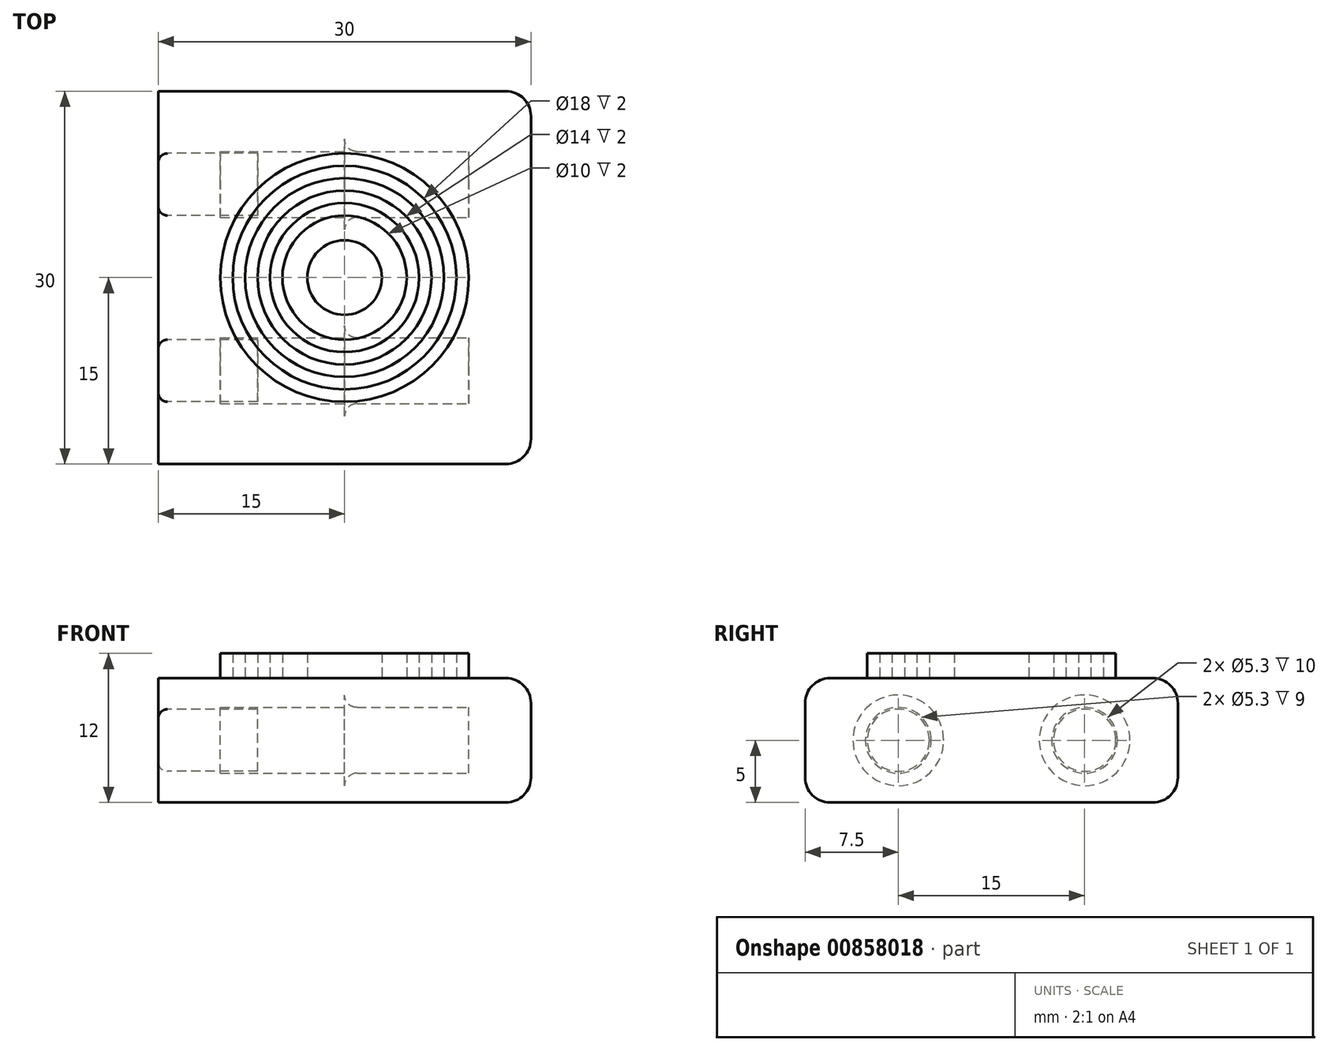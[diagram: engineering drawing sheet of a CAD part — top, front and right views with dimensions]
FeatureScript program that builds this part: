
annotation { "Feature Type Name" : "Feature", "Feature Type Description" : "" }
export const myFeature = defineFeature(function(context is Context, id is Id, definition is map)
    precondition{}
    {
        {
            var Q0;
            Q0=qCreatedBy(makeId("Right.planeOp"),FACE);
            var sketch = newSketch(context, id + "F0", { "sketchPlane" : qUnion([Q0])});
            skLineSegment(sketch, "E0.bottom", {"start": v(-15, 5) * mm, "end": v(15, 5) * mm});
            skLineSegment(sketch, "E0.top", {"start": v(-15, -5) * mm, "end": v(15, -5) * mm});
            skLineSegment(sketch, "E0.left", {"start": v(-15, 5) * mm, "end": v(-15, -5) * mm});
            skLineSegment(sketch, "E0.right", {"start": v(15, 5) * mm, "end": v(15, -5) * mm});
            skPoint(sketch, "E0.middle", {"position": v(0, 0) * mm});
            skLineSegment(sketch, "E1", {"start": v(-15, 0) * mm, "end": v(0, 0) * mm, "construction": true});
            skLineSegment(sketch, "E2", {"start": v(0, 0) * mm, "end": v(15, 0) * mm, "construction": true});
            skCircle(sketch, "E3", {"center": v(-7.5, 0) * mm, "radius": 2.65 * mm});
            skCircle(sketch, "E4", {"center": v(7.5, 0) * mm, "radius": 2.65 * mm});
            skSolve(sketch);
        }
        {
            var Q0;
            Q0=makeQuery(id+"F0.imprint","IMPRINT",FACE,{"disambiguationData":[TD([[makeQuery(id+"F0.imprint","IMPRINT",EDGE,{"derivedFrom":sQuery(id+"F0.wireOp",EDGE,"E0.bottom")}),-1.0]])]});
            var Q1;
            Q1=makeQuery(id+"F0.imprint","IMPRINT",FACE,{"disambiguationData":[TD([[makeQuery(id+"F0.imprint","IMPRINT",EDGE,{"derivedFrom":sQuery(id+"F0.wireOp",EDGE,"E4")}),1.0]])]});
            var Q2;
            Q2=makeQuery(id+"F0.imprint","IMPRINT",FACE,{"disambiguationData":[TD([[makeQuery(id+"F0.imprint","IMPRINT",EDGE,{"derivedFrom":sQuery(id+"F0.wireOp",EDGE,"E3")}),1.0]])]});
            extrude(context, id + "F1", {"entities" : qUnion([Q0, Q1, Q2]), "endBound" : BoundingType.SYMMETRIC, "depth" : 20 * mm, "offsetDistance" : 25 * mm});
        }
        {
            var Q0;
            Q0=makeQuery(id+"F1.opExtrude","SWEPT_BODY",BODY,{"disambiguationData":[OSD([sQuery(id+"F0.wireOp",EDGE,"E0.bottom"),sQuery(id+"F0.wireOp",EDGE,"E0.top"),sQuery(id+"F0.wireOp",EDGE,"E0.left"),sQuery(id+"F0.wireOp",EDGE,"E0.right")])]});
            transform(context, id + "F2", {"entities" : qUnion([Q0]), "transformType" : TransformType.TRANSLATION_3D, "dx" : -25 * mm, "dy" : 0 * mm, "dz" : 0 * mm, "makeCopy" : true});
        }
        {
            var Q0;
            Q0=makeQuery(id+"F2.opPattern","COPY",FACE,{"derivedFrom":makeQuery(id+"F1.opExtrude","CAP_FACE",FACE,{"disambiguationData":[OSD([sQuery(id+"F0.wireOp",EDGE,"E0.bottom"),sQuery(id+"F0.wireOp",EDGE,"E0.top"),sQuery(id+"F0.wireOp",EDGE,"E0.left"),sQuery(id+"F0.wireOp",EDGE,"E0.right")])],"isStart":true}),"instanceName":"1"});
            extrude(context, id + "F3", {"entities" : qUnion([Q0]), "operationType" : NewBodyOperationType.REMOVE, "oppositeDirection" : true, "depth" : 5 * mm, "offsetDistance" : 25 * mm});
        }
        {
            var Q0;
            Q0=makeQuery(id+"F1.opExtrude","CAP_FACE",FACE,{"disambiguationData":[OSD([sQuery(id+"F0.wireOp",EDGE,"E0.bottom"),sQuery(id+"F0.wireOp",EDGE,"E0.top"),sQuery(id+"F0.wireOp",EDGE,"E0.left"),sQuery(id+"F0.wireOp",EDGE,"E0.right")])],"isStart":false});
            extrude(context, id + "F4", {"entities" : qUnion([Q0]), "operationType" : NewBodyOperationType.REMOVE, "oppositeDirection" : true, "depth" : 5 * mm, "offsetDistance" : 25 * mm});
        }
        {
            var Q0;
            Q0=makeQuery(id+"F0.imprint","IMPRINT",FACE,{"disambiguationData":[TD([[makeQuery(id+"F0.imprint","IMPRINT",EDGE,{"derivedFrom":sQuery(id+"F0.wireOp",EDGE,"E4")}),1.0]])]});
            var Q1;
            Q1=makeQuery(id+"F0.imprint","IMPRINT",FACE,{"disambiguationData":[TD([[makeQuery(id+"F0.imprint","IMPRINT",EDGE,{"derivedFrom":sQuery(id+"F0.wireOp",EDGE,"E3")}),1.0]])]});
            extrude(context, id + "F5", {"entities" : qUnion([Q0, Q1]), "operationType" : NewBodyOperationType.REMOVE, "oppositeDirection" : true, "depth" : 25 * mm, "offsetDistance" : 25 * mm});
        }
        {
            var Q0;
            Q0=makeQuery(id+"F5.boolean.opBoolean","INTERSECT",EDGE,{"derivedFrom":[makeQuery(id+"F1.opExtrude","CAP_FACE",FACE,{"disambiguationData":[OSD([sQuery(id+"F0.wireOp",EDGE,"E0.bottom"),sQuery(id+"F0.wireOp",EDGE,"E0.top"),sQuery(id+"F0.wireOp",EDGE,"E0.left"),sQuery(id+"F0.wireOp",EDGE,"E0.right")])],"isStart":true}),makeQuery(id+"F5.opExtrude","SWEPT_FACE",FACE,{"disambiguationData":[OSD([sQuery(id+"F0.wireOp",EDGE,"E4")])]})]});
            var Q1;
            Q1=makeQuery(id+"F5.boolean.opBoolean","INTERSECT",EDGE,{"derivedFrom":[makeQuery(id+"F1.opExtrude","CAP_FACE",FACE,{"disambiguationData":[OSD([sQuery(id+"F0.wireOp",EDGE,"E0.bottom"),sQuery(id+"F0.wireOp",EDGE,"E0.top"),sQuery(id+"F0.wireOp",EDGE,"E0.left"),sQuery(id+"F0.wireOp",EDGE,"E0.right")])],"isStart":true}),makeQuery(id+"F5.opExtrude","SWEPT_FACE",FACE,{"disambiguationData":[OSD([sQuery(id+"F0.wireOp",EDGE,"E3")])]})]});
            fillet(context, id + "F6", {"entities" : qUnion([Q0, Q1]), "radius" : 1 * mm, "tangentPropagation" : true, "allowEdgeOverflow" : false});
        }
        {
            var Q0;
            Q0=makeQuery(id+"F2.opPattern","COPY",FACE,{"derivedFrom":makeQuery(id+"F1.opExtrude","CAP_FACE",FACE,{"disambiguationData":[OSD([sQuery(id+"F0.wireOp",EDGE,"E0.bottom"),sQuery(id+"F0.wireOp",EDGE,"E0.top"),sQuery(id+"F0.wireOp",EDGE,"E0.left"),sQuery(id+"F0.wireOp",EDGE,"E0.right")])],"isStart":false}),"instanceName":"1"});
            var sketch = newSketch(context, id + "F7", { "sketchPlane" : qUnion([Q0])});
            skLineSegment(sketch, "E5.bottom", {"start": v(-15, 5) * mm, "end": v(15, 5) * mm});
            skLineSegment(sketch, "E5.top", {"start": v(-15, -5) * mm, "end": v(15, -5) * mm});
            skLineSegment(sketch, "E5.left", {"start": v(-15, 5) * mm, "end": v(-15, -5) * mm});
            skLineSegment(sketch, "E5.right", {"start": v(15, 5) * mm, "end": v(15, -5) * mm});
            skPoint(sketch, "E5.middle", {"position": v(0, 0) * mm});
            skLineSegment(sketch, "E6", {"start": v(-15, 0) * mm, "end": v(0, 0) * mm, "construction": true});
            skLineSegment(sketch, "E7", {"start": v(0, 0) * mm, "end": v(15, 0) * mm, "construction": true});
            skCircle(sketch, "E8", {"center": v(-7.5, 0) * mm, "radius": 2.5 * mm});
            skCircle(sketch, "E9", {"center": v(7.5, 0) * mm, "radius": 2.5 * mm});
            skSolve(sketch);
        }
        {
            var Q0;
            Q0=makeQuery(id+"F7.imprint","IMPRINT",FACE,{"disambiguationData":[TD([[makeQuery(id+"F7.imprint","IMPRINT",EDGE,{"derivedFrom":sQuery(id+"F7.wireOp",EDGE,"E8")}),1.0]])]});
            var Q1;
            Q1=makeQuery(id+"F7.imprint","IMPRINT",FACE,{"disambiguationData":[TD([[makeQuery(id+"F7.imprint","IMPRINT",EDGE,{"derivedFrom":sQuery(id+"F7.wireOp",EDGE,"E9")}),1.0]])]});
            extrude(context, id + "F8", {"entities" : qUnion([Q0, Q1]), "operationType" : NewBodyOperationType.ADD, "depth" : 8 * mm, "offsetDistance" : 25 * mm});
        }
        {
            var Q0;
            Q0=makeQuery(id+"F8.opExtrude","CAP_EDGE",EDGE,{"disambiguationData":[OSD([sQuery(id+"F7.wireOp",EDGE,"E8")])],"isStart":true});
            var Q1;
            Q1=makeQuery(id+"F8.opExtrude","CAP_EDGE",EDGE,{"disambiguationData":[OSD([sQuery(id+"F7.wireOp",EDGE,"E9")])],"isStart":true});
            fillet(context, id + "F9", {"entities" : qUnion([Q0, Q1]), "radius" : 0.75 * mm, "tangentPropagation" : true, "allowEdgeOverflow" : false});
        }
        {
            var Q0;
            Q0=makeQuery(id+"F1.opExtrude","SWEPT_BODY",BODY,{"disambiguationData":[OSD([sQuery(id+"F0.wireOp",EDGE,"E0.bottom"),sQuery(id+"F0.wireOp",EDGE,"E0.top"),sQuery(id+"F0.wireOp",EDGE,"E0.left"),sQuery(id+"F0.wireOp",EDGE,"E0.right")])]});
            var Q1;
            Q1=qCreatedBy(makeId("Right.planeOp"),FACE);
            transform(context, id + "F10", {"entities" : qUnion([Q0]), "transformType" : TransformType.TRANSLATION_DISTANCE, "transformDirection" : qUnion([Q1]), "distance" : 10 * mm, "makeCopy" : false});
        }
        {
            var Q0;
            Q0=makeQuery(id+"F2.opPattern","COPY",BODY,{"derivedFrom":makeQuery(id+"F1.opExtrude","SWEPT_BODY",BODY,{"disambiguationData":[OSD([sQuery(id+"F0.wireOp",EDGE,"E0.bottom"),sQuery(id+"F0.wireOp",EDGE,"E0.top"),sQuery(id+"F0.wireOp",EDGE,"E0.left"),sQuery(id+"F0.wireOp",EDGE,"E0.right")])]}),"instanceName":"1"});
            var Q1;
            Q1=qCreatedBy(makeId("Right.planeOp"),FACE);
            transform(context, id + "F11", {"entities" : qUnion([Q0]), "transformType" : TransformType.TRANSLATION_DISTANCE, "transformDirection" : qUnion([Q1]), "distance" : 15 * mm, "makeCopy" : false});
        }
        {
            var Q0;
            Q0=makeQuery(id+"F1.opExtrude","SWEPT_FACE",FACE,{"disambiguationData":[OSD([sQuery(id+"F0.wireOp",EDGE,"E0.bottom")])]});
            var sketch = newSketch(context, id + "F12", { "sketchPlane" : qUnion([Q0])});
            skCircle(sketch, "E10", {"center": v(0, 0) * mm, "radius": 10 * mm});
            skCircle(sketch, "E11", {"center": v(0, 0) * mm, "radius": 9 * mm});
            skCircle(sketch, "E12", {"center": v(0, 0) * mm, "radius": 8 * mm});
            skCircle(sketch, "E13", {"center": v(0, 0) * mm, "radius": 7 * mm});
            skCircle(sketch, "E14", {"center": v(0, 0) * mm, "radius": 6 * mm});
            skCircle(sketch, "E15", {"center": v(0, 0) * mm, "radius": 5 * mm});
            skLineSegment(sketch, "E16", {"start": v(0, 10) * mm, "end": v(0, -10) * mm});
            skCircle(sketch, "E17", {"center": v(0, 0) * mm, "radius": 3 * mm});
            skSolve(sketch);
        }
        {
            var Q0;
            {var subQ0=sQuery(id+"F12.wireOp",EDGE,"E16");var subQ5=sQuery(id+"F12.wireOp",EDGE,"E11");var subQ6=makeQuery(id+"F12.imprint","INTERSECT",VERTEX,{"disambiguationData":[OD(0.0)],"derivedFrom":[subQ5,subQ0]});Q0=makeQuery(id+"F12.imprint","IMPRINT",FACE,{"disambiguationData":[TD([[makeQuery(id+"F12.imprint","IMPRINT",EDGE,{"disambiguationData":[TD([[subQ6,-1.0]])],"derivedFrom":subQ5}),-1.0]])]});}
            var Q1;
            {var subQ0=sQuery(id+"F12.wireOp",EDGE,"E16");var subQ1=sQuery(id+"F12.wireOp",EDGE,"E12");var subQ2=makeQuery(id+"F12.imprint","INTERSECT",VERTEX,{"disambiguationData":[OD(0.0)],"derivedFrom":[subQ1,subQ0]});Q1=makeQuery(id+"F12.imprint","IMPRINT",FACE,{"disambiguationData":[TD([[makeQuery(id+"F12.imprint","IMPRINT",EDGE,{"disambiguationData":[TD([[subQ2,-1.0]])],"derivedFrom":subQ1}),1.0]])]});}
            var Q2;
            {var subQ0=sQuery(id+"F12.wireOp",EDGE,"E16");var subQ1=sQuery(id+"F12.wireOp",EDGE,"E14");var subQ2=makeQuery(id+"F12.imprint","INTERSECT",VERTEX,{"disambiguationData":[OD(0.0)],"derivedFrom":[subQ1,subQ0]});Q2=makeQuery(id+"F12.imprint","IMPRINT",FACE,{"disambiguationData":[TD([[makeQuery(id+"F12.imprint","IMPRINT",EDGE,{"disambiguationData":[TD([[subQ2,-1.0]])],"derivedFrom":subQ1}),1.0]])]});}
            var Q3;
            {var subQ0=sQuery(id+"F12.wireOp",EDGE,"E17");var subQ1=sQuery(id+"F12.wireOp",EDGE,"E16");var subQ2=makeQuery(id+"F12.imprint","INTERSECT",VERTEX,{"disambiguationData":[OD(0.0)],"derivedFrom":[subQ1,subQ0]});Q3=makeQuery(id+"F12.imprint","IMPRINT",FACE,{"disambiguationData":[TD([[makeQuery(id+"F12.imprint","IMPRINT",EDGE,{"disambiguationData":[TD([[subQ2,-1.0]])],"derivedFrom":subQ1}),-1.0]])]});}
            extrude(context, id + "F13", {"entities" : qUnion([Q0, Q1, Q2, Q3]), "operationType" : NewBodyOperationType.ADD, "depth" : 2 * mm, "offsetDistance" : 25 * mm});
        }
        {
            var Q0;
            {var subQ0=sQuery(id+"F12.wireOp",EDGE,"E16");var subQ5=sQuery(id+"F12.wireOp",EDGE,"E11");var subQ6=makeQuery(id+"F12.imprint","INTERSECT",VERTEX,{"disambiguationData":[OD(0.0)],"derivedFrom":[subQ5,subQ0]});Q0=makeQuery(id+"F12.imprint","IMPRINT",FACE,{"disambiguationData":[TD([[makeQuery(id+"F12.imprint","IMPRINT",EDGE,{"disambiguationData":[TD([[subQ6,1.0]])],"derivedFrom":subQ5}),-1.0]])]});}
            var Q1;
            {var subQ0=sQuery(id+"F12.wireOp",EDGE,"E16");var subQ1=sQuery(id+"F12.wireOp",EDGE,"E12");var subQ2=makeQuery(id+"F12.imprint","INTERSECT",VERTEX,{"disambiguationData":[OD(0.0)],"derivedFrom":[subQ1,subQ0]});Q1=makeQuery(id+"F12.imprint","IMPRINT",FACE,{"disambiguationData":[TD([[makeQuery(id+"F12.imprint","IMPRINT",EDGE,{"disambiguationData":[TD([[subQ2,1.0]])],"derivedFrom":subQ1}),1.0]])]});}
            var Q2;
            {var subQ0=sQuery(id+"F12.wireOp",EDGE,"E16");var subQ1=sQuery(id+"F12.wireOp",EDGE,"E14");var subQ2=makeQuery(id+"F12.imprint","INTERSECT",VERTEX,{"disambiguationData":[OD(0.0)],"derivedFrom":[subQ1,subQ0]});Q2=makeQuery(id+"F12.imprint","IMPRINT",FACE,{"disambiguationData":[TD([[makeQuery(id+"F12.imprint","IMPRINT",EDGE,{"disambiguationData":[TD([[subQ2,1.0]])],"derivedFrom":subQ1}),1.0]])]});}
            var Q3;
            {var subQ0=sQuery(id+"F12.wireOp",EDGE,"E17");var subQ1=sQuery(id+"F12.wireOp",EDGE,"E16");var subQ2=makeQuery(id+"F12.imprint","INTERSECT",VERTEX,{"disambiguationData":[OD(0.0)],"derivedFrom":[subQ1,subQ0]});Q3=makeQuery(id+"F12.imprint","IMPRINT",FACE,{"disambiguationData":[TD([[makeQuery(id+"F12.imprint","IMPRINT",EDGE,{"disambiguationData":[TD([[subQ2,-1.0]])],"derivedFrom":subQ1}),1.0]])]});}
            extrude(context, id + "F14", {"entities" : qUnion([Q0, Q1, Q2, Q3]), "operationType" : NewBodyOperationType.ADD, "depth" : 2 * mm, "offsetDistance" : 25 * mm});
        }
        {
            var Q0;
            Q0=makeQuery(id+"F3.boolean.opBoolean","COPY",EDGE,{"derivedFrom":makeQuery(id+"F3.opExtrude","CAP_EDGE",EDGE,{"disambiguationData":[OSD([sQuery(id+"F0.wireOp",EDGE,"E0.right")])],"isStart":false})});
            var Q1;
            Q1=makeQuery(id+"F2.opPattern","COPY",EDGE,{"derivedFrom":makeQuery(id+"F1.opExtrude","SWEPT_EDGE",EDGE,{"disambiguationData":[OSD([sQuery(id+"F0.wireOp",EDGE,"E0.top"),sQuery(id+"F0.wireOp",EDGE,"E0.right")])]}),"instanceName":"1"});
            var Q2;
            Q2=makeQuery(id+"F2.opPattern","COPY",EDGE,{"derivedFrom":makeQuery(id+"F1.opExtrude","SWEPT_EDGE",EDGE,{"disambiguationData":[OSD([sQuery(id+"F0.wireOp",EDGE,"E0.bottom"),sQuery(id+"F0.wireOp",EDGE,"E0.right")])]}),"instanceName":"1"});
            var Q3;
            Q3=makeQuery(id+"F3.boolean.opBoolean","COPY",EDGE,{"derivedFrom":makeQuery(id+"F3.opExtrude","CAP_EDGE",EDGE,{"disambiguationData":[OSD([sQuery(id+"F0.wireOp",EDGE,"E0.bottom")])],"isStart":false})});
            var Q4;
            Q4=makeQuery(id+"F3.boolean.opBoolean","COPY",EDGE,{"derivedFrom":makeQuery(id+"F3.opExtrude","CAP_EDGE",EDGE,{"disambiguationData":[OSD([sQuery(id+"F0.wireOp",EDGE,"E0.top")])],"isStart":false})});
            var Q5;
            Q5=makeQuery(id+"F2.opPattern","COPY",EDGE,{"derivedFrom":makeQuery(id+"F1.opExtrude","SWEPT_EDGE",EDGE,{"disambiguationData":[OSD([sQuery(id+"F0.wireOp",EDGE,"E0.bottom"),sQuery(id+"F0.wireOp",EDGE,"E0.left")])]}),"instanceName":"1"});
            var Q6;
            Q6=makeQuery(id+"F2.opPattern","COPY",EDGE,{"derivedFrom":makeQuery(id+"F1.opExtrude","SWEPT_EDGE",EDGE,{"disambiguationData":[OSD([sQuery(id+"F0.wireOp",EDGE,"E0.top"),sQuery(id+"F0.wireOp",EDGE,"E0.left")])]}),"instanceName":"1"});
            var Q7;
            Q7=makeQuery(id+"F3.boolean.opBoolean","COPY",EDGE,{"derivedFrom":makeQuery(id+"F3.opExtrude","CAP_EDGE",EDGE,{"disambiguationData":[OSD([sQuery(id+"F0.wireOp",EDGE,"E0.left")])],"isStart":false})});
            var Q8;
            Q8=makeQuery(id+"F1.opExtrude","SWEPT_EDGE",EDGE,{"disambiguationData":[OSD([sQuery(id+"F0.wireOp",EDGE,"E0.bottom"),sQuery(id+"F0.wireOp",EDGE,"E0.left")])]});
            var Q9;
            Q9=makeQuery(id+"F1.opExtrude","SWEPT_EDGE",EDGE,{"disambiguationData":[OSD([sQuery(id+"F0.wireOp",EDGE,"E0.top"),sQuery(id+"F0.wireOp",EDGE,"E0.left")])]});
            var Q10;
            Q10=makeQuery(id+"F4.boolean.opBoolean","COPY",FACE,{"derivedFrom":makeQuery(id+"F4.opExtrude","CAP_FACE",FACE,{"disambiguationData":[OSD([sQuery(id+"F0.wireOp",EDGE,"E0.bottom"),sQuery(id+"F0.wireOp",EDGE,"E0.top"),sQuery(id+"F0.wireOp",EDGE,"E0.left"),sQuery(id+"F0.wireOp",EDGE,"E0.right")])],"isStart":false})});
            var Q11;
            Q11=makeQuery(id+"F1.opExtrude","SWEPT_EDGE",EDGE,{"disambiguationData":[OSD([sQuery(id+"F0.wireOp",EDGE,"E0.bottom"),sQuery(id+"F0.wireOp",EDGE,"E0.right")])]});
            var Q12;
            Q12=makeQuery(id+"F1.opExtrude","SWEPT_EDGE",EDGE,{"disambiguationData":[OSD([sQuery(id+"F0.wireOp",EDGE,"E0.top"),sQuery(id+"F0.wireOp",EDGE,"E0.right")])]});
            fillet(context, id + "F15", {"entities" : qUnion([Q0, Q1, Q2, Q3, Q4, Q5, Q6, Q7, Q8, Q9, Q10, Q11, Q12]), "radius" : 2 * mm, "tangentPropagation" : true, "allowEdgeOverflow" : false});
        }
    });
